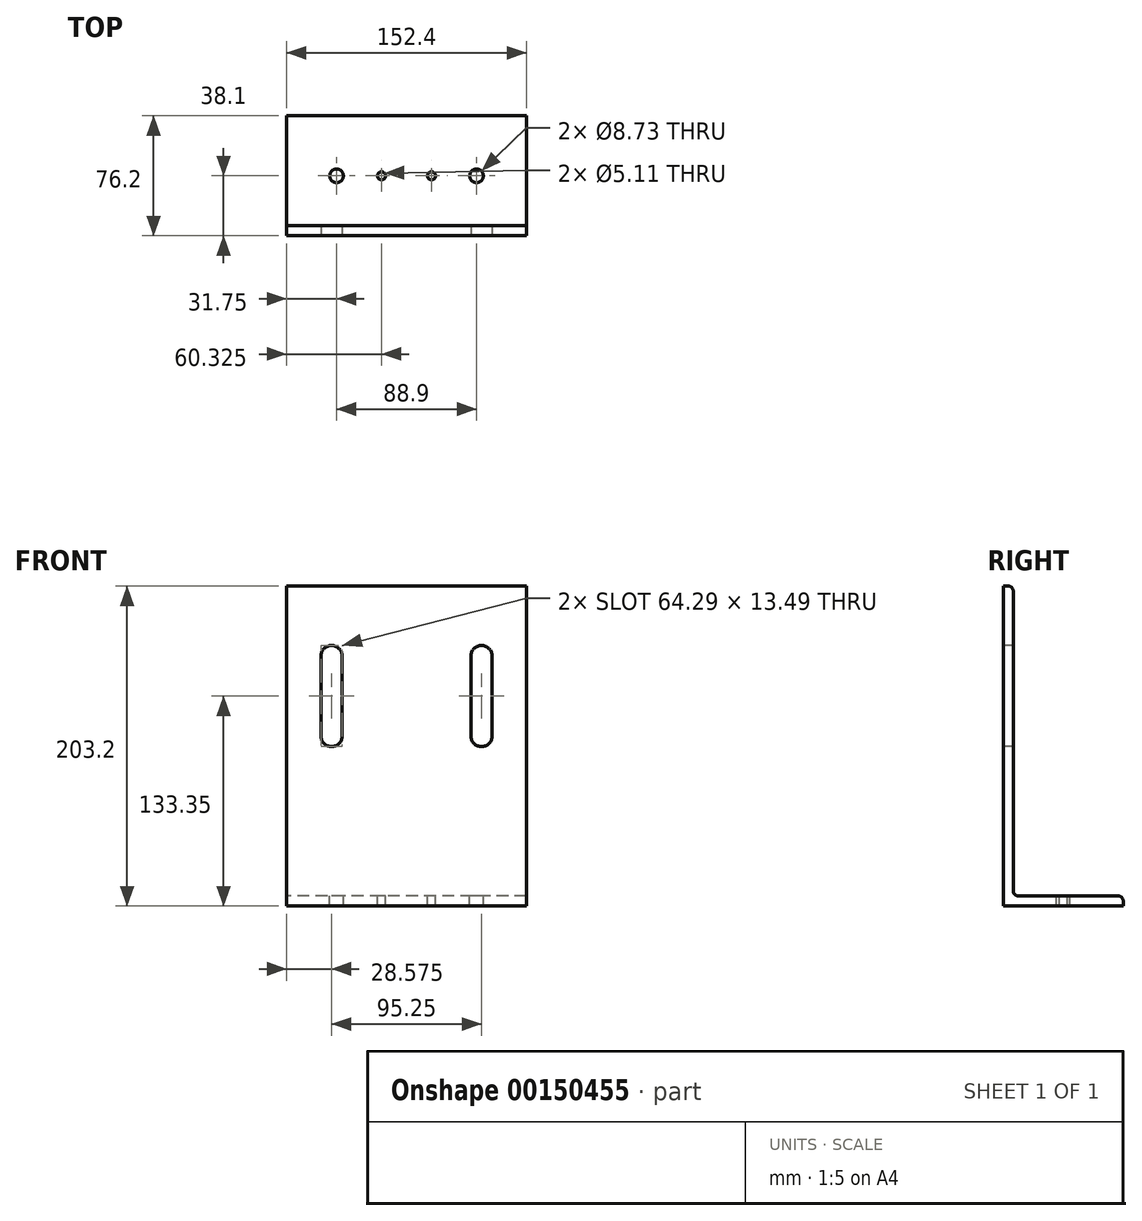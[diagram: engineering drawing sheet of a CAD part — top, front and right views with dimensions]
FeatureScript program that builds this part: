
annotation { "Feature Type Name" : "Feature", "Feature Type Description" : "" }
export const myFeature = defineFeature(function(context is Context, id is Id, definition is map)
    precondition{}
    {
        {
            var Q0;
            Q0=qCreatedBy(makeId("Right.planeOp"),FACE);
            var sketch = newSketch(context, id + "F0", { "sketchPlane" : qUnion([Q0])});
            skLineSegment(sketch, "E0", {"start": v(0, 203.2) * mm, "end": v(0, 0) * mm});
            skLineSegment(sketch, "E1", {"start": v(0, 0) * mm, "end": v(76.2, 0) * mm});
            skLineSegment(sketch, "E2.0", {"start": v(6.35, 6.35) * mm, "end": v(76.2, 6.35) * mm});
            skLineSegment(sketch, "E2.1", {"start": v(6.35, 203.2) * mm, "end": v(6.35, 6.35) * mm});
            skLineSegment(sketch, "E3", {"start": v(76.2, 6.35) * mm, "end": v(76.2, 0) * mm});
            skLineSegment(sketch, "E4", {"start": v(6.35, 203.2) * mm, "end": v(0, 203.2) * mm});
            skSolve(sketch);
        }
        {
            var Q0;
            Q0 = qSketchRegion(id + "F0", true);
            extrude(context, id + "F1", {"entities" : qUnion([Q0]), "endBound" : BoundingType.SYMMETRIC, "depth" : 152.4 * mm});
        }
        {
            var Q0;
            Q0=makeQuery(id+"F1.opExtrude","SWEPT_FACE",FACE,{"disambiguationData":[OSD([sQuery(id+"F0.wireOp",EDGE,"E0")])]});
            var sketch = newSketch(context, id + "F2", { "sketchPlane" : qUnion([Q0])});
            skLineSegment(sketch, "E5", {"start": v(-47.62, 158.75) * mm, "end": v(-47.62, 107.95) * mm, "construction": true});
            skArc(sketch, "E6.0.startCap", {"start": v(-54.37, 158.75) * mm, "mid": v(-47.62, 165.5) * mm, "end": v(-40.88, 158.75) * mm});
            skArc(sketch, "E6.0.endCap", {"start": v(-40.88, 107.95) * mm, "mid": v(-47.63, 101.2) * mm, "end": v(-54.37, 107.95) * mm});
            skLineSegment(sketch, "E6.0.left", {"start": v(-40.88, 158.75) * mm, "end": v(-40.88, 107.95) * mm});
            skLineSegment(sketch, "E6.0.right", {"start": v(-54.37, 158.75) * mm, "end": v(-54.37, 107.95) * mm});
            skArc(sketch, "E7.MirrorCS", {"start": v(54.37, 158.75) * mm, "mid": v(47.62, 165.5) * mm, "end": v(40.88, 158.75) * mm});
            skLineSegment(sketch, "E8.MirrorCS", {"start": v(54.37, 158.75) * mm, "end": v(54.37, 107.95) * mm});
            skArc(sketch, "E9.MirrorCS", {"start": v(40.88, 107.95) * mm, "mid": v(47.63, 101.2) * mm, "end": v(54.37, 107.95) * mm});
            skLineSegment(sketch, "E10.MirrorCS", {"start": v(40.88, 158.75) * mm, "end": v(40.88, 107.95) * mm});
            skSolve(sketch);
        }
        {
            var Q0;
            Q0 = qSketchRegion(id + "F2", true);
            extrude(context, id + "F3", {"entities" : qUnion([Q0]), "operationType" : NewBodyOperationType.REMOVE, "oppositeDirection" : true, "depth" : 25.4 * mm});
        }
        {
            var Q0;
            Q0=makeQuery(id+"F1.opExtrude","SWEPT_FACE",FACE,{"disambiguationData":[OSD([sQuery(id+"F0.wireOp",EDGE,"E2.0")])]});
            var sketch = newSketch(context, id + "F4", { "sketchPlane" : qUnion([Q0])});
            skPoint(sketch, "E11", {"position": v(44.45, 38.1) * mm});
            skPoint(sketch, "E12", {"position": v(-44.45, 38.1) * mm});
            skLineSegment(sketch, "E13", {"start": v(0, -702.53) * mm, "end": v(0, 6.35) * mm, "construction": true});
            skPoint(sketch, "E13.endSnap0", {"position": v(0, 6.35) * mm});
            skSolve(sketch);
        }
        {
            var Q0;
            Q0=sQuery(id+"F4.wireOp",VERTEX,"E12");
            var Q1;
            Q1=sQuery(id+"F4.wireOp",VERTEX,"E11");
            var Q2;
            Q2=makeQuery(id+"F1.opExtrude","SWEPT_BODY",BODY,{"disambiguationData":[OSD([sQuery(id+"F0.wireOp",EDGE,"E0"),sQuery(id+"F0.wireOp",EDGE,"E1"),sQuery(id+"F0.wireOp",EDGE,"E2.0"),sQuery(id+"F0.wireOp",EDGE,"E2.1"),sQuery(id+"F0.wireOp",EDGE,"E3"),sQuery(id+"F0.wireOp",EDGE,"E4")])]});
            hole(context, id + "F5", {"style" : HoleStyle.SIMPLE, "endStyle" : HoleEndStyle.THROUGH, "holeDiameter" : 8.73 * mm, "isTappedThrough" : true, "tappedDepth" : 12.7 * mm, "tapClearance" : 3, "locations" : qUnion([Q0, Q1]), "scope" : qUnion([Q2])});
        }
        {
            var Q0;
            Q0=makeQuery(id+"F1.opExtrude","SWEPT_FACE",FACE,{"disambiguationData":[OSD([sQuery(id+"F0.wireOp",EDGE,"E2.0")])]});
            var sketch = newSketch(context, id + "F6", { "sketchPlane" : qUnion([Q0])});
            skPoint(sketch, "E14", {"position": v(-15.88, 38.1) * mm});
            skPoint(sketch, "E15", {"position": v(15.88, 38.1) * mm});
            skPoint(sketch, "E16", {"position": v(-44.45, 38.1) * mm});
            skSolve(sketch);
        }
        {
            var Q0;
            Q0=sQuery(id+"F6.wireOp",VERTEX,"E15");
            var Q1;
            Q1=sQuery(id+"F6.wireOp",VERTEX,"E14");
            var Q2;
            Q2=makeQuery(id+"F1.opExtrude","SWEPT_BODY",BODY,{"disambiguationData":[OSD([sQuery(id+"F0.wireOp",EDGE,"E0"),sQuery(id+"F0.wireOp",EDGE,"E1"),sQuery(id+"F0.wireOp",EDGE,"E2.0"),sQuery(id+"F0.wireOp",EDGE,"E2.1"),sQuery(id+"F0.wireOp",EDGE,"E3"),sQuery(id+"F0.wireOp",EDGE,"E4")])]});
            hole(context, id + "F7", {"style" : HoleStyle.SIMPLE, "endStyle" : HoleEndStyle.THROUGH, "standardTappedOrClearance" : lookupTablePath({ "standard" : "ANSI", "engagement" : "75%", "pitch" : "20 tpi", "size" : "1/4", "type" : "Tapped" }), "standardBlindInLast" : lookupTablePath({ "standard" : "ANSI", "engagement" : "75%", "pitch" : "20 tpi", "size" : "1/4", "type" : "Tapped" }), "holeDiameter" : 5.1 * mm, "majorDiameter" : 6.35 * mm, "showTappedDepth" : true, "isTappedThrough" : true, "tappedDepth" : 12.7 * mm, "tapClearance" : 3, "locations" : qUnion([Q0, Q1]), "scope" : qUnion([Q2])});
        }
        {
            var Q0;
            Q0=makeQuery(id+"F1.opExtrude","SWEPT_EDGE",EDGE,{"disambiguationData":[OSD([sQuery(id+"F0.wireOp",EDGE,"E2.0"),sQuery(id+"F0.wireOp",EDGE,"E2.1")])]});
            var Q1;
            Q1=makeQuery(id+"F1.opExtrude","SWEPT_EDGE",EDGE,{"disambiguationData":[OSD([sQuery(id+"F0.wireOp",EDGE,"E2.1"),sQuery(id+"F0.wireOp",EDGE,"E4")])]});
            var Q2;
            Q2=makeQuery(id+"F1.opExtrude","SWEPT_EDGE",EDGE,{"disambiguationData":[OSD([sQuery(id+"F0.wireOp",EDGE,"E2.0"),sQuery(id+"F0.wireOp",EDGE,"E3")])]});
            fillet(context, id + "F8", {"entities" : qUnion([Q0, Q1, Q2]), "radius" : 3.17 * mm, "tangentPropagation" : true, "allowEdgeOverflow" : false});
        }
    });
